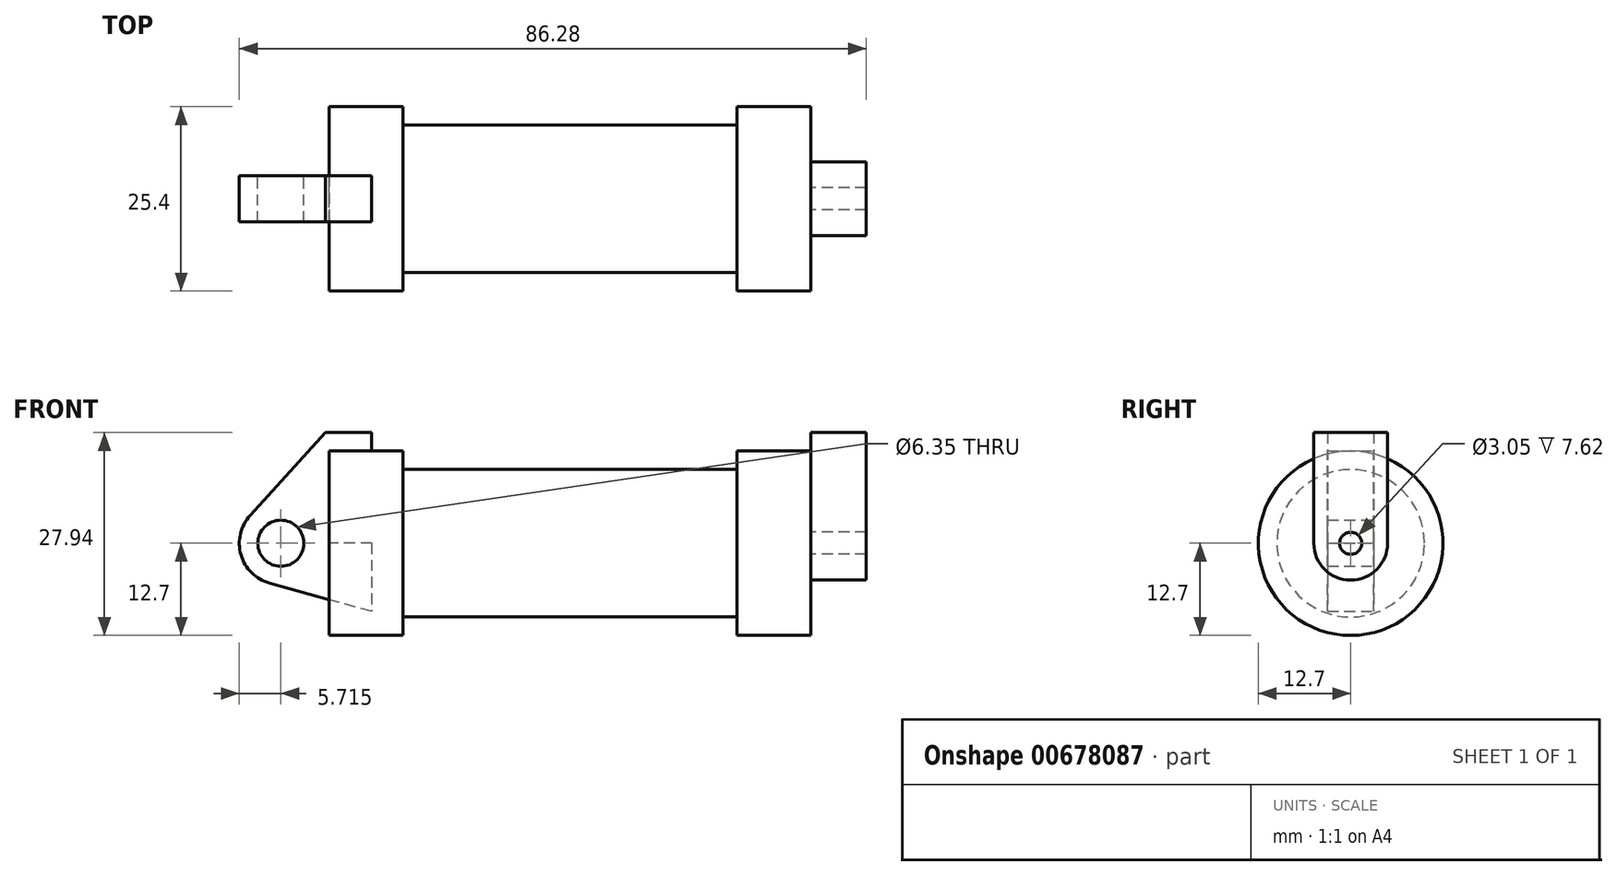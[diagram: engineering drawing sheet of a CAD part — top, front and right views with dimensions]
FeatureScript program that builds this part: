
annotation { "Feature Type Name" : "Feature", "Feature Type Description" : "" }
export const myFeature = defineFeature(function(context is Context, id is Id, definition is map)
    precondition{}
    {
        {
            var Q0;
            Q0=qCreatedBy(makeId("Front.planeOp"),FACE);
            var sketch = newSketch(context, id + "F0", { "sketchPlane" : qUnion([Q0])});
            skLineSegment(sketch, "E0", {"start": v(0, 0) * mm, "end": v(0, 12.7) * mm});
            skLineSegment(sketch, "E1", {"start": v(0, 12.7) * mm, "end": v(10.16, 12.7) * mm});
            skLineSegment(sketch, "E2", {"start": v(10.16, 12.7) * mm, "end": v(10.16, 10.16) * mm});
            skLineSegment(sketch, "E3", {"start": v(10.16, 10.16) * mm, "end": v(56.13, 10.16) * mm});
            skLineSegment(sketch, "E4", {"start": v(56.13, 10.16) * mm, "end": v(56.13, 12.7) * mm});
            skLineSegment(sketch, "E5", {"start": v(56.13, 12.7) * mm, "end": v(66.3, 12.7) * mm});
            skLineSegment(sketch, "E6", {"start": v(66.3, 12.7) * mm, "end": v(66.3, 0) * mm});
            skLineSegment(sketch, "E7", {"start": v(66.3, 0) * mm, "end": v(0, 0) * mm});
            skLineSegment(sketch, "E8", {"start": v(5.84, 15.24) * mm, "end": v(-0.5, 15.24) * mm});
            skLineSegment(sketch, "E9", {"start": v(-0.5, 15.24) * mm, "end": v(-10.88, 3.85) * mm});
            skLineSegment(sketch, "E10", {"start": v(0, 0) * mm, "end": v(-6.65, 0) * mm});
            skCircle(sketch, "E11", {"center": v(-6.65, 0) * mm, "radius": 5.72 * mm});
            skCircle(sketch, "E12", {"center": v(-6.65, 0) * mm, "radius": 3.18 * mm});
            skLineSegment(sketch, "E13", {"start": v(5.84, 15.24) * mm, "end": v(5.84, -9.4) * mm});
            skLineSegment(sketch, "E14", {"start": v(5.84, -9.4) * mm, "end": v(-8.18, -5.5) * mm});
            skSolve(sketch);
        }
        {
            var Q0;
            {var subQ0=sQuery(id+"F0.wireOp",EDGE,"E2");Q0=makeQuery(id+"F0.imprint","IMPRINT",FACE,{"disambiguationData":[TD([[makeQuery(id+"F0.imprint","IMPRINT",EDGE,{"derivedFrom":subQ0}),-1.0]])]});}
            var Q1;
            {var subQ0=sQuery(id+"F0.wireOp",EDGE,"E0");Q1=makeQuery(id+"F0.imprint","IMPRINT",FACE,{"disambiguationData":[TD([[makeQuery(id+"F0.imprint","IMPRINT",EDGE,{"derivedFrom":subQ0}),-1.0]])]});}
            var Q2;
            Q2=sQuery(id+"F0.wireOp",EDGE,"E7");
            revolve(context, id + "F1", {"entities" : qUnion([Q0, Q1]), "axis" : qUnion([Q2]), "revolveType" : RevolveType.FULL});
        }
        {
            var Q0;
            {var subQ5=sQuery(id+"F0.wireOp",EDGE,"E12");Q0=makeQuery(id+"F0.imprint","IMPRINT",FACE,{"disambiguationData":[TD([[makeQuery(id+"F0.imprint","IMPRINT",EDGE,{"derivedFrom":subQ5}),-1.0]])]});}
            var Q1;
            {var subQ1=sQuery(id+"F0.wireOp",EDGE,"E0");Q1=makeQuery(id+"F0.imprint","IMPRINT",FACE,{"disambiguationData":[TD([[makeQuery(id+"F0.imprint","IMPRINT",EDGE,{"derivedFrom":subQ1}),1.0]])]});}
            var Q2;
            {var subQ0=sQuery(id+"F0.wireOp",EDGE,"E14");Q2=makeQuery(id+"F0.imprint","IMPRINT",FACE,{"disambiguationData":[TD([[makeQuery(id+"F0.imprint","IMPRINT",EDGE,{"derivedFrom":subQ0}),-1.0]])]});}
            extrude(context, id + "F2", {"entities" : qUnion([Q0, Q1, Q2]), "endBound" : BoundingType.SYMMETRIC, "depth" : 6.35 * mm, "offsetDistance" : 25.4 * mm, "hasSecondDirection" : true, "secondDirectionOppositeDirection" : true, "secondDirectionDepth" : 25.4 * mm});
        }
        {
            var Q0;
            Q0=makeQuery(id+"F1.opRevolve","SWEPT_FACE",FACE,{"disambiguationData":[OSD([sQuery(id+"F0.wireOp",EDGE,"E6")])]});
            var sketch = newSketch(context, id + "F3", { "sketchPlane" : qUnion([Q0])});
            skCircle(sketch, "E15", {"center": v(0, 0) * mm, "radius": 1.52 * mm});
            skCircle(sketch, "E16", {"center": v(0, 0) * mm, "radius": 5.08 * mm});
            skLineSegment(sketch, "E17", {"start": v(-5.08, 0) * mm, "end": v(-5.08, 15.24) * mm});
            skLineSegment(sketch, "E18", {"start": v(5.08, 0) * mm, "end": v(5.08, 15.24) * mm});
            skLineSegment(sketch, "E19", {"start": v(-5.08, 15.24) * mm, "end": v(5.08, 15.24) * mm});
            skSolve(sketch);
        }
        {
            var Q0;
            {var subQ0=sQuery(id+"F3.wireOp",EDGE,"E17");var subQ1=sQuery(id+"F3.wireOp",EDGE,"E16");var subQ2=makeQuery(id+"F3.imprint","INTERSECT",VERTEX,{"derivedFrom":[subQ1,subQ0]});Q0=makeQuery(id+"F3.imprint","IMPRINT",FACE,{"disambiguationData":[TD([[makeQuery(id+"F3.imprint","IMPRINT",EDGE,{"disambiguationData":[TD([[subQ2,1.0]])],"derivedFrom":subQ1}),-1.0]])]});}
            var Q1;
            {var subQ0=sQuery(id+"F3.wireOp",EDGE,"E19");Q1=makeQuery(id+"F3.imprint","IMPRINT",FACE,{"disambiguationData":[TD([[makeQuery(id+"F3.imprint","IMPRINT",EDGE,{"derivedFrom":subQ0}),-1.0]])]});}
            var Q2;
            Q2=makeQuery(id+"F3.imprint","IMPRINT",FACE,{"disambiguationData":[TD([[makeQuery(id+"F3.imprint","IMPRINT",EDGE,{"derivedFrom":sQuery(id+"F3.wireOp",EDGE,"E15")}),-1.0]])]});
            extrude(context, id + "F4", {"entities" : qUnion([Q0, Q1, Q2]), "operationType" : NewBodyOperationType.ADD, "depth" : 7.62 * mm, "offsetDistance" : 25.4 * mm});
        }
        {
            var Q0;
            Q0=makeQuery(id+"F4.opExtrude","SWEPT_FACE",FACE,{"disambiguationData":[OSD([sQuery(id+"F3.wireOp",EDGE,"E19")])]});
            var sketch = newSketch(context, id + "F5", { "sketchPlane" : qUnion([Q0])});
            skCircle(sketch, "E20", {"center": v(70.1, -0.02) * mm, "radius": 1.52 * mm});
            skPoint(sketch, "E20.centerSnap0", {"position": v(70.1, 5.08) * mm});
            skSolve(sketch);
        }
        {
            var Q0;
            Q0=makeQuery(id+"F2.opExtrude","SWEPT_FACE",FACE,{"disambiguationData":[OSD([sQuery(id+"F0.wireOp",EDGE,"E8")])]});
            var sketch = newSketch(context, id + "F6", { "sketchPlane" : qUnion([Q0])});
            skCircle(sketch, "E21", {"center": v(2.67, 0) * mm, "radius": 1.52 * mm});
            skPoint(sketch, "E21.centerSnap0", {"position": v(5.84, 0) * mm});
            skPoint(sketch, "E21.centerSnap1", {"position": v(2.67, 3.18) * mm});
            skSolve(sketch);
        }
        {
            var Q0;
            Q0=sQuery(id+"F6.wireOp",EDGE,"E21");
            extrude(context, id + "F7", {"bodyType" : ToolBodyType.SURFACE, "surfaceEntities" : qUnion([Q0]), "oppositeDirection" : true, "depth" : 17.78 * mm, "offsetDistance" : 25.4 * mm});
        }
        {
            var Q0;
            Q0=sQuery(id+"F5.wireOp",EDGE,"E20");
            extrude(context, id + "F8", {"bodyType" : ToolBodyType.SURFACE, "surfaceEntities" : qUnion([Q0]), "oppositeDirection" : true, "depth" : 10.4 * mm, "offsetDistance" : 25.4 * mm});
        }
    });
